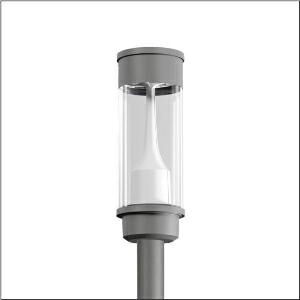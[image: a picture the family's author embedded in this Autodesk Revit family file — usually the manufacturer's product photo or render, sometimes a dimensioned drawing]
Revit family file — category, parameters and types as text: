
# Revit family: litepole_iq___p1_0a_5xa5415bf14h_51c2
name_source: partatom
category: Lighting Fixtures
units: mm (PartAtom-declared; Revit-internal decimal feet)

## family parameters
Cut with Voids When Loaded = No
Host = Face
Light Source = No
Part Type = Normal
Room Calculation Point = No
Round Connector Dimension = Use Diameter
Shared = No

## types (1)
- --- (1 x LED, 1510 lm, 12.9 W, 2200K)
    Apparent Load = 13 VA
    CIE Flux Codes = 32 61 90 93 100
    Color Rendering = 70
    Color Temperature = 2200K
    Default Elevation = 1800 mm
    Description = Litepole iQ, mast luminaire, Module 540 iQ-SR, primary light control with 3 zone facetted reflector, of plastic, silver coated, highly specular, structured, primary optical cover: cover, of PMMA, transparent, partly coated, light distribution: P1.0a, light emission: direct distribution, primary light characteristic: strongly asymmetric, installation type: post-top, LED, High Power LED, rated luminous flux: 1.510lm, luminous efficacy: 117lm/W, light colour: 722, colour temperature: 2200K, control gear: ECG iQ, control: optimised constant luminous flux control (CLO 2.0), Desk-Remote (wireless, voltage-free reading and setting of iQ features in the workshop via application-optimized NFC function/RFID function), Light-Fading, Smart-Wire, Night-Set, Lumen-Switch, Temp-Guard, Auto-Match, Street-Remote, presetting dimming logarithmic, with terminal, 6-pole, max. 2.5mm², mains connection: 230..240V, AC, 50/60Hz, start of lifetime: 13W, end of service life: 13W, reduction: 6W, luminaire housing, upper part, of glass-fibre reinforced polyester, coated, Siteco® metallic grey (DB 702S), diameter: 210mm, height: 590mm, spigot size: d x l = 76 x 70mm (post-top) | with reducer (optional accessory) 60 x 70mm, post-top mast mounting element, of diecast aluminium, coated, Siteco® metallic grey (DB 702S), Module 540 iQ-SR, traffic white (RAL 9016), equipment: standard, protection rating (complete): IP65, insulation class (complete): insulation class II (safety insulation), certification: CE, ENEC, VDE, packaging unit: 1 piece

Light Distribution: P1.0a
    Height = 590 mm
    Lamp = 1 x LED
    Lamp Light Flux = 1510 lm
    Lamp Power = 12.9 W
    Lamp count = 1
    Length = 220 mm
    Luminous efficacy = 117 lm/W
    Manufacturer = Siteco
    ModVariant = No
    Model = 5XA5415BF14H
    Number of Poles = 1
    OnlyDefault = Yes
    Power Factor = 1
    Product Name = Litepole iQ | P1.0a
    Product group = mast luminaire | pylon top
    ProductGroupID = 6100
    Protection Class = Protection class II
    Protection Degree = IP 65
    RLX_Detail_Level = 1
    RLX_Emergency_Light_Flux = 0 lm
    RLX_Emergency_Type = 0
    RLX_Emergency_Type_DB = No
    RlxData = <blob elided: 64125 chars, md5=9966c6fb>
    Socket = socket
    Standby Power = 0 W
    System Light Flux = 1510 lm
    System Power = 13 W
    Type Comments = factory setting: luminous flux: 100 % | dim-lin: 254 | 516 mA
    Type Image = l_1006025.jpg
    URL = http://relux.com
    VarID = @adj_091085
    Voltage = 0 V
    Weight = 0.00 kg
    Width = 0 mm  [stored 0 ft]

note: [stored X ft] marks values corroborated as IEEE doubles in the binary element streams (Revit-internal decimal feet)

## geometry (parser evidence)
native form markers: Blend x4, Sweep x14
no freeform markers — native parametric forms only
